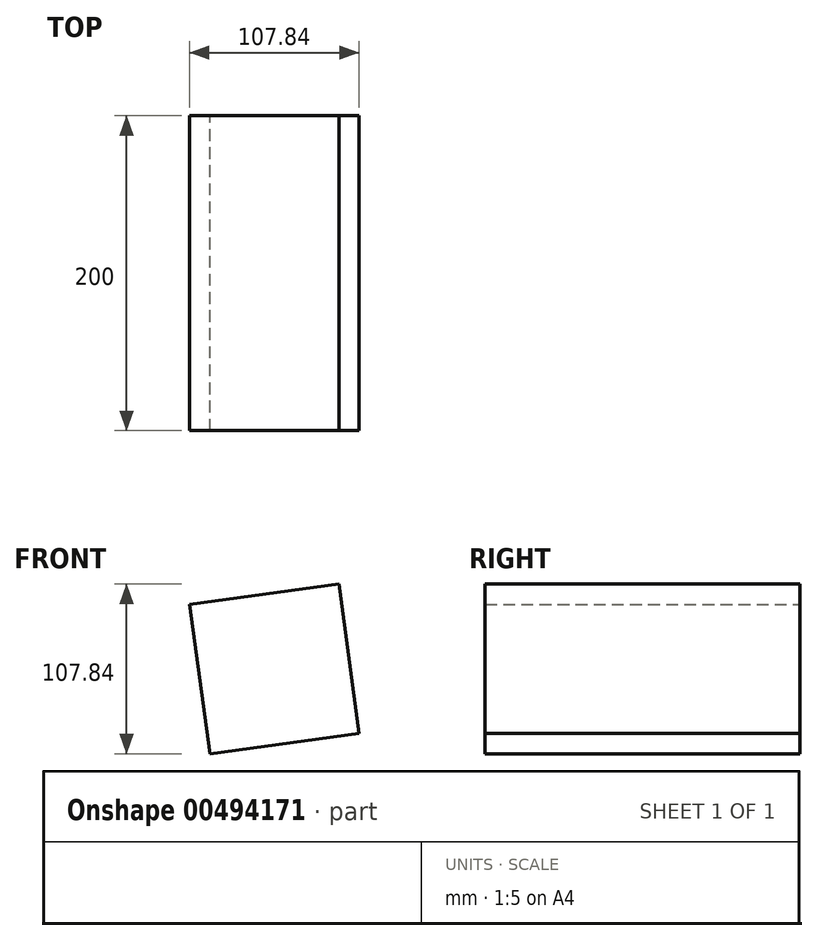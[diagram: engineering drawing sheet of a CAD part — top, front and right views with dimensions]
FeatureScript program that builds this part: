
annotation { "Feature Type Name" : "Feature", "Feature Type Description" : "" }
export const myFeature = defineFeature(function(context is Context, id is Id, definition is map)
    precondition{}
    {
        {
            var Q0;
            Q0=qCreatedBy(makeId("Front.planeOp"),FACE);
            var sketch = newSketch(context, id + "F0", { "sketchPlane" : qUnion([Q0])});
            skCircle(sketch, "E0.cCircle", {"center": v(0, 0) * mm, "radius": 67.71 * mm, "construction": true});
            skLineSegment(sketch, "E0.0", {"start": v(-53.92, 40.95) * mm, "end": v(40.95, 53.92) * mm});
            skLineSegment(sketch, "E0.1", {"start": v(40.95, 53.92) * mm, "end": v(53.92, -40.95) * mm});
            skLineSegment(sketch, "E0.2", {"start": v(53.92, -40.95) * mm, "end": v(-40.95, -53.92) * mm});
            skLineSegment(sketch, "E0.3", {"start": v(-40.95, -53.92) * mm, "end": v(-53.92, 40.95) * mm});
            skSolve(sketch);
        }
        {
            var Q0;
            Q0=makeQuery(id+"F0.imprint","IMPRINT",FACE,{"disambiguationData":[TD([[makeQuery(id+"F0.imprint","IMPRINT",EDGE,{"derivedFrom":sQuery(id+"F0.wireOp",EDGE,"E0.0")}),-1.0]])]});
            extrude(context, id + "F1", {"entities" : qUnion([Q0]), "endBound" : BoundingType.SYMMETRIC, "depth" : 200 * mm});
        }
    });
